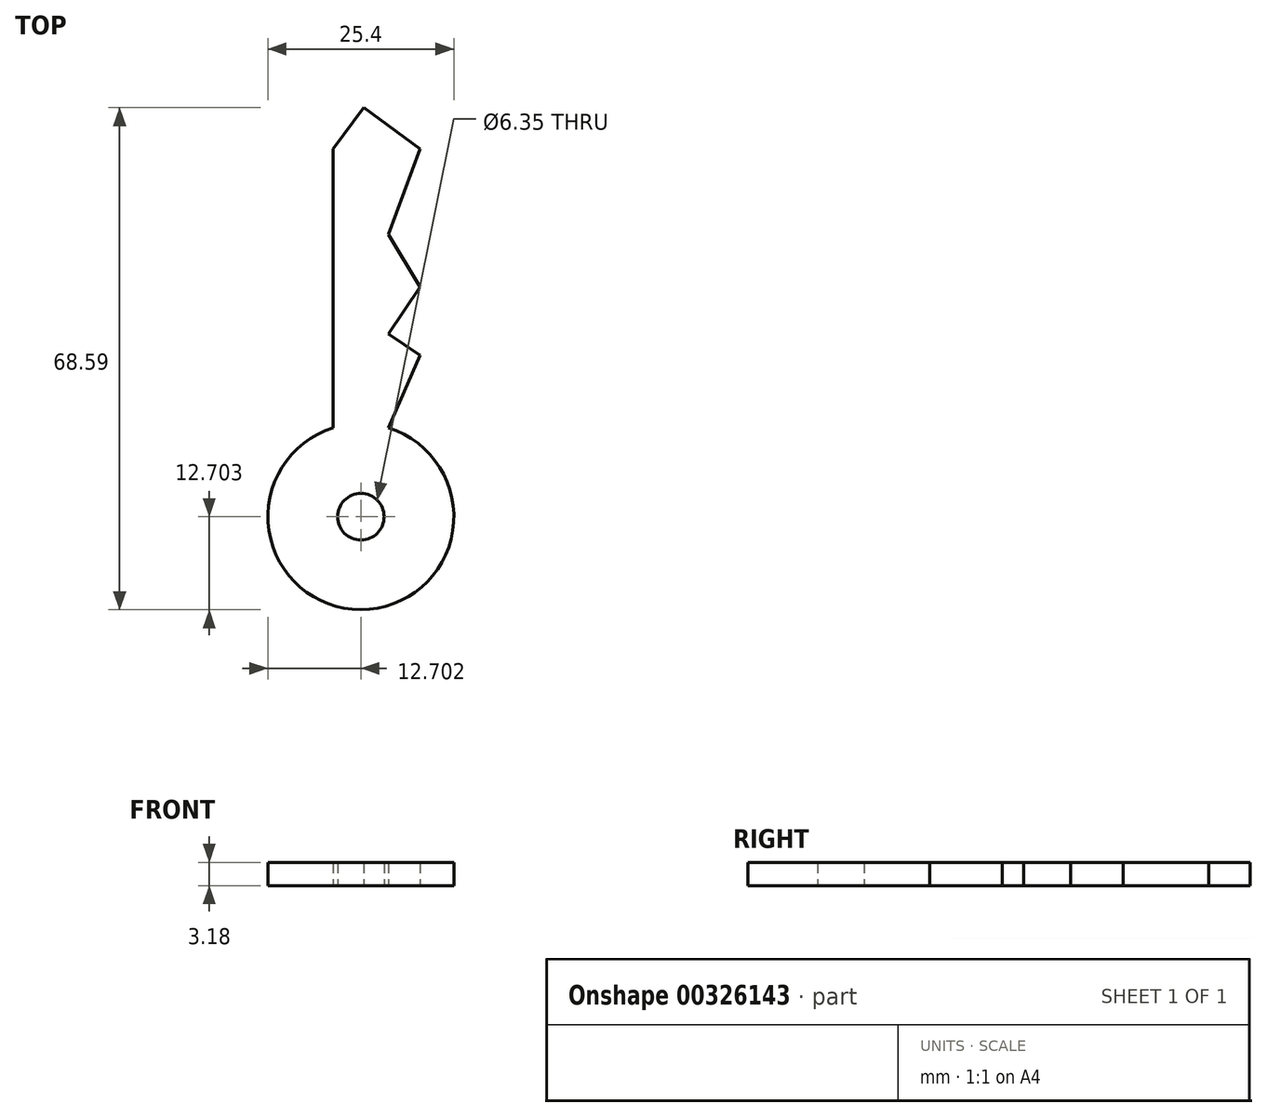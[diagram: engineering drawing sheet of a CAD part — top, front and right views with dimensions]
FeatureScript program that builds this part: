
annotation { "Feature Type Name" : "Feature", "Feature Type Description" : "" }
export const myFeature = defineFeature(function(context is Context, id is Id, definition is map)
    precondition{}
    {
        {
            var Q0;
            Q0=qCreatedBy(makeId("Top.planeOp"),FACE);
            var sketch = newSketch(context, id + "F0", { "sketchPlane" : qUnion([Q0])});
            skLineSegment(sketch, "E0", {"start": v(0, 0) * mm, "end": v(0, 38.1) * mm});
            skLineSegment(sketch, "E1", {"start": v(0, 38.1) * mm, "end": v(4.15, 43.76) * mm});
            skLineSegment(sketch, "E2", {"start": v(4.15, 43.76) * mm, "end": v(11.87, 38.1) * mm});
            skLineSegment(sketch, "E3", {"start": v(11.87, 38.1) * mm, "end": v(7.54, 26.4) * mm});
            skLineSegment(sketch, "E4", {"start": v(7.54, 26.4) * mm, "end": v(11.87, 19.24) * mm});
            skLineSegment(sketch, "E5", {"start": v(11.87, 19.24) * mm, "end": v(7.54, 12.83) * mm});
            skLineSegment(sketch, "E6", {"start": v(7.54, 12.83) * mm, "end": v(11.87, 9.91) * mm});
            skLineSegment(sketch, "E7", {"start": v(11.87, 9.91) * mm, "end": v(7.54, 0) * mm});
            skArc(sketch, "E8", {"start": v(0, 0) * mm, "mid": v(3.77, -24.83) * mm, "end": v(7.54, 0) * mm});
            skCircle(sketch, "E9", {"center": v(3.77, -12.13) * mm, "radius": 3.18 * mm});
            skSolve(sketch);
        }
        {
            var Q0;
            Q0 = qSketchRegion(id + "F0", true);
            extrude(context, id + "F1", {"entities" : qUnion([Q0]), "depth" : 3.17 * mm});
        }
    });
